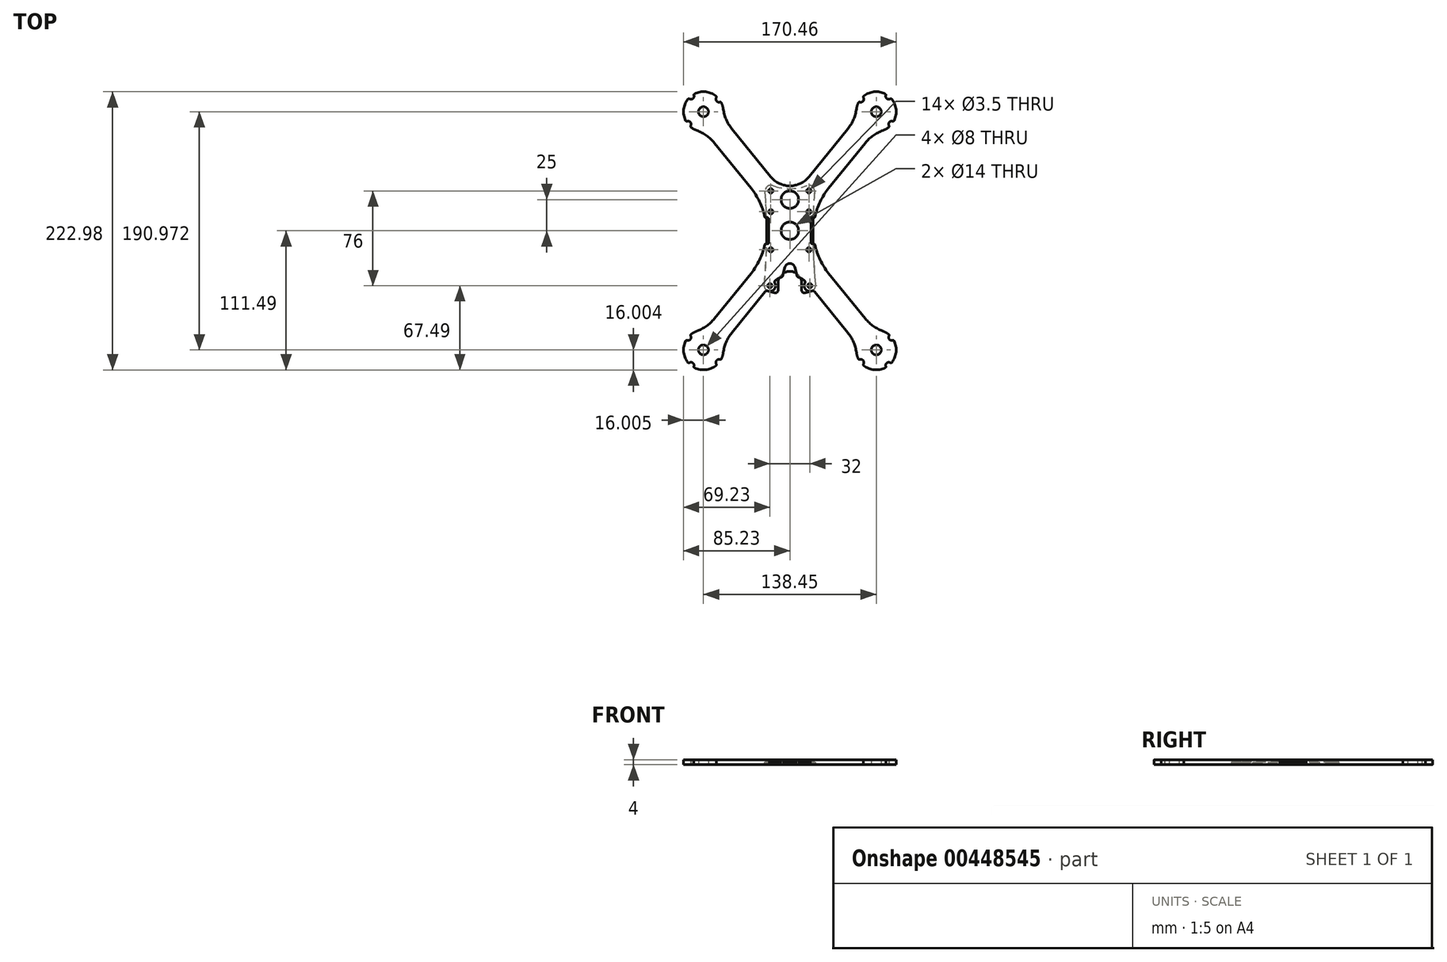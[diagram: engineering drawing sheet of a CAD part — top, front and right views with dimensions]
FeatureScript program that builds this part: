
annotation { "Feature Type Name" : "Feature", "Feature Type Description" : "" }
export const myFeature = defineFeature(function(context is Context, id is Id, definition is map)
    precondition{}
    {
        {
            var Q0;
            Q0=qCreatedBy(makeId("Top.planeOp"),FACE);
            var sketch = newSketch(context, id + "F0", { "sketchPlane" : qUnion([Q0])});
            skLineSegment(sketch, "E0", {"start": v(0, 10) * mm, "end": v(-69.23, 95.49) * mm, "construction": true});
            skCircle(sketch, "E1", {"center": v(-15.25, 32) * mm, "radius": 1.75 * mm});
            skCircle(sketch, "E2", {"center": v(-15.25, 15.25) * mm, "radius": 1.75 * mm});
            skLineSegment(sketch, "E3", {"start": v(-60.51, 70.42) * mm, "end": v(-31.06, 34.05) * mm});
            skLineSegment(sketch, "E4", {"start": v(-46.52, 81.75) * mm, "end": v(-15.44, 43.36) * mm});
            skLineSegment(sketch, "E5", {"start": v(-19.21, 10.5) * mm, "end": v(-18, 10.5) * mm});
            skArc(sketch, "E6", {"start": v(-53.37, 97.62) * mm, "mid": v(-53.93, 100.2) * mm, "end": v(-54.92, 102.64) * mm});
            skLineSegment(sketch, "E7.trimOffspring", {"start": v(-67.9, 79.54) * mm, "end": v(-67.9, 79.54) * mm});
            skCircle(sketch, "E8", {"center": v(-69.23, 95.49) * mm, "radius": 14 * mm, "construction": true});
            skCircle(sketch, "E9", {"center": v(-69.23, 95.49) * mm, "radius": 4 * mm});
            skArc(sketch, "E10", {"start": v(-20.2, 11.3) * mm, "mid": v(-24.28, 23.31) * mm, "end": v(-31.06, 34.05) * mm});
            skPoint(sketch, "E11.orphan", {"position": v(-19, 0) * mm});
            skArc(sketch, "E12", {"start": v(-15.44, 43.36) * mm, "mid": v(-8.55, 37.93) * mm, "end": v(0, 36) * mm});
            skPoint(sketch, "E13.visualSharp", {"position": v(-20.03, 10.5) * mm});
            skArc(sketch, "E13.filletArc", {"start": v(-20.2, 11.3) * mm, "mid": v(-19.84, 10.72) * mm, "end": v(-19.21, 10.5) * mm});
            skPoint(sketch, "E14.visualSharp", {"position": v(-53.9, 90.87) * mm});
            skArc(sketch, "E14.filletArc", {"start": v(-53.37, 97.62) * mm, "mid": v(-51.04, 89.22) * mm, "end": v(-46.52, 81.75) * mm});
            skPoint(sketch, "E15.visualSharp", {"position": v(-67.9, 79.54) * mm});
            skArc(sketch, "E15.filletArc", {"start": v(-60.51, 70.42) * mm, "mid": v(-66.87, 76.4) * mm, "end": v(-74.61, 80.42) * mm});
            skArc(sketch, "E16", {"start": v(-80.48, 105.72) * mm, "mid": v(-77.72, 105.98) * mm, "end": v(-76.9, 108.62) * mm});
            skArc(sketch, "E17", {"start": v(-59, 106.74) * mm, "mid": v(-58.73, 103.98) * mm, "end": v(-56.09, 103.16) * mm});
            skArc(sketch, "E18", {"start": v(-79.46, 84.23) * mm, "mid": v(-79.72, 87) * mm, "end": v(-82.36, 87.82) * mm});
            skLineSegment(sketch, "E19", {"start": v(-69.23, 95.49) * mm, "end": v(-79.3, 107.92) * mm, "construction": true});
            skLineSegment(sketch, "E20", {"start": v(-69.23, 95.49) * mm, "end": v(-56.8, 105.56) * mm, "construction": true});
            skLineSegment(sketch, "E21", {"start": v(-69.23, 95.49) * mm, "end": v(-81.66, 85.42) * mm, "construction": true});
            skArc(sketch, "E22.trimOffspring", {"start": v(-59.25, 108) * mm, "mid": v(-67.55, 111.4) * mm, "end": v(-76.38, 109.8) * mm});
            skArc(sketch, "E23.trimOffspring", {"start": v(-81.73, 105.46) * mm, "mid": v(-85.14, 97.16) * mm, "end": v(-83.54, 88.33) * mm});
            skArc(sketch, "E24.trimOffspring", {"start": v(-79.2, 82.98) * mm, "mid": v(-77.01, 81.5) * mm, "end": v(-74.61, 80.42) * mm});
            skPoint(sketch, "E25.visualSharp", {"position": v(-77.23, 109.34) * mm});
            skArc(sketch, "E25.filletArc", {"start": v(-76.38, 109.8) * mm, "mid": v(-76.85, 109.3) * mm, "end": v(-76.9, 108.62) * mm});
            skPoint(sketch, "E26.visualSharp", {"position": v(-81.1, 106.2) * mm});
            skArc(sketch, "E26.filletArc", {"start": v(-80.48, 105.72) * mm, "mid": v(-81.15, 105.82) * mm, "end": v(-81.73, 105.46) * mm});
            skPoint(sketch, "E27.visualSharp", {"position": v(-83.08, 87.48) * mm});
            skArc(sketch, "E27.filletArc", {"start": v(-83.54, 88.33) * mm, "mid": v(-83.04, 87.86) * mm, "end": v(-82.36, 87.82) * mm});
            skPoint(sketch, "E28.visualSharp", {"position": v(-79.94, 83.6) * mm});
            skArc(sketch, "E28.filletArc", {"start": v(-79.46, 84.23) * mm, "mid": v(-79.56, 83.56) * mm, "end": v(-79.2, 82.98) * mm});
            skPoint(sketch, "E29.visualSharp", {"position": v(-58.51, 107.37) * mm});
            skArc(sketch, "E29.filletArc", {"start": v(-59, 106.74) * mm, "mid": v(-58.9, 107.41) * mm, "end": v(-59.25, 108) * mm});
            skPoint(sketch, "E30.visualSharp", {"position": v(-55.37, 103.5) * mm});
            skArc(sketch, "E30.filletArc", {"start": v(-54.92, 102.64) * mm, "mid": v(-55.4, 103.11) * mm, "end": v(-56.09, 103.16) * mm});
            skLineSegment(sketch, "E31", {"start": v(-17, 9.5) * mm, "end": v(-17, 0) * mm});
            skPoint(sketch, "E32.visualSharp", {"position": v(-17, 10.5) * mm});
            skArc(sketch, "E32.filletArc", {"start": v(-17, 9.5) * mm, "mid": v(-17.3, 10.2) * mm, "end": v(-18, 10.5) * mm});
            skArc(sketch, "E33.MirrorCS", {"start": v(-83.54, -88.33) * mm, "mid": v(-83.04, -87.86) * mm, "end": v(-82.36, -87.82) * mm});
            skArc(sketch, "E34.MirrorCS", {"start": v(-59, -106.74) * mm, "mid": v(-58.9, -107.41) * mm, "end": v(-59.25, -108) * mm});
            skArc(sketch, "E35.MirrorCS", {"start": v(-80.48, -105.72) * mm, "mid": v(-81.15, -105.82) * mm, "end": v(-81.73, -105.46) * mm});
            skArc(sketch, "E36.MirrorCS", {"start": v(-79.46, -84.23) * mm, "mid": v(-79.72, -87) * mm, "end": v(-82.36, -87.82) * mm});
            skArc(sketch, "E37.MirrorCS", {"start": v(-80.48, -105.72) * mm, "mid": v(-77.72, -105.98) * mm, "end": v(-76.9, -108.62) * mm});
            skArc(sketch, "E38.MirrorCS", {"start": v(-17, -9.5) * mm, "mid": v(-17.3, -10.2) * mm, "end": v(-18, -10.5) * mm});
            skArc(sketch, "E39.MirrorCS", {"start": v(-79.46, -84.23) * mm, "mid": v(-79.56, -83.56) * mm, "end": v(-79.2, -82.98) * mm});
            skArc(sketch, "E40.MirrorCS", {"start": v(-76.38, -109.8) * mm, "mid": v(-76.85, -109.3) * mm, "end": v(-76.9, -108.62) * mm});
            skArc(sketch, "E41.MirrorCS", {"start": v(-20.2, -11.3) * mm, "mid": v(-19.84, -10.72) * mm, "end": v(-19.21, -10.5) * mm});
            skArc(sketch, "E42.MirrorCS", {"start": v(-54.92, -102.64) * mm, "mid": v(-55.4, -103.11) * mm, "end": v(-56.09, -103.16) * mm});
            skArc(sketch, "E43.MirrorCS", {"start": v(-59, -106.74) * mm, "mid": v(-58.73, -103.98) * mm, "end": v(-56.09, -103.16) * mm});
            skLineSegment(sketch, "E44.MirrorCS", {"start": v(-19.21, -10.5) * mm, "end": v(-18, -10.5) * mm});
            skArc(sketch, "E45.MirrorCS", {"start": v(-53.37, -97.62) * mm, "mid": v(-53.93, -100.2) * mm, "end": v(-54.92, -102.64) * mm});
            skArc(sketch, "E46.MirrorCS", {"start": v(-79.2, -82.98) * mm, "mid": v(-77.01, -81.5) * mm, "end": v(-74.61, -80.42) * mm});
            skCircle(sketch, "E47.MirrorC", {"center": v(-15.25, -15.25) * mm, "radius": 1.75 * mm});
            skLineSegment(sketch, "E48.MirrorCS", {"start": v(-69.23, -95.49) * mm, "end": v(-81.66, -85.42) * mm, "construction": true});
            skArc(sketch, "E49.MirrorCS", {"start": v(-53.37, -97.62) * mm, "mid": v(-51.04, -89.22) * mm, "end": v(-46.52, -81.75) * mm});
            skLineSegment(sketch, "E50.MirrorCS", {"start": v(-69.23, -95.49) * mm, "end": v(-56.8, -105.56) * mm, "construction": true});
            skLineSegment(sketch, "E51.MirrorCS", {"start": v(-17, -9.5) * mm, "end": v(-17, 0) * mm});
            skPoint(sketch, "E52.MirrorP", {"position": v(-81.1, -106.2) * mm});
            skArc(sketch, "E53.MirrorCS", {"start": v(-20.2, -11.3) * mm, "mid": v(-24.28, -23.31) * mm, "end": v(-31.06, -34.05) * mm});
            skPoint(sketch, "E54.MirrorP", {"position": v(-55.37, -103.5) * mm});
            skLineSegment(sketch, "E55.MirrorCS", {"start": v(-60.51, -70.42) * mm, "end": v(-31.06, -34.05) * mm});
            skPoint(sketch, "E56.MirrorP", {"position": v(-83.08, -87.48) * mm});
            skPoint(sketch, "E57.MirrorP", {"position": v(-53.9, -90.87) * mm});
            skPoint(sketch, "E58.MirrorP", {"position": v(-58.51, -107.37) * mm});
            skPoint(sketch, "E59.MirrorP", {"position": v(-77.23, -109.34) * mm});
            skArc(sketch, "E60.MirrorCS", {"start": v(-81.73, -105.46) * mm, "mid": v(-85.14, -97.16) * mm, "end": v(-83.54, -88.33) * mm});
            skLineSegment(sketch, "E61.MirrorCS", {"start": v(-67.9, -79.54) * mm, "end": v(-67.9, -79.54) * mm});
            skCircle(sketch, "E62.MirrorC", {"center": v(-69.23, -95.49) * mm, "radius": 14 * mm, "construction": true});
            skLineSegment(sketch, "E63.MirrorCS", {"start": v(0, -10) * mm, "end": v(-69.23, -95.49) * mm, "construction": true});
            skArc(sketch, "E64.MirrorCS", {"start": v(-60.51, -70.42) * mm, "mid": v(-66.87, -76.4) * mm, "end": v(-74.61, -80.42) * mm});
            skPoint(sketch, "E65.MirrorP", {"position": v(-67.9, -79.54) * mm});
            skPoint(sketch, "E66.MirrorP", {"position": v(-17, -10.5) * mm});
            skPoint(sketch, "E67.MirrorP", {"position": v(-79.94, -83.6) * mm});
            skArc(sketch, "E68.MirrorCS", {"start": v(-59.25, -108) * mm, "mid": v(-67.55, -111.4) * mm, "end": v(-76.38, -109.8) * mm});
            skCircle(sketch, "E69.MirrorC", {"center": v(-69.23, -95.49) * mm, "radius": 4 * mm});
            skLineSegment(sketch, "E70.MirrorCS", {"start": v(-46.52, -81.75) * mm, "end": v(-19.86, -48.82) * mm});
            skLineSegment(sketch, "E71.MirrorCS", {"start": v(-69.23, -95.49) * mm, "end": v(-79.3, -107.92) * mm, "construction": true});
            skPoint(sketch, "E72.MirrorP", {"position": v(-20.03, -10.5) * mm});
            skCircle(sketch, "E73", {"center": v(-16, -44) * mm, "radius": 1.75 * mm});
            skArc(sketch, "E74", {"start": v(-17.6, -48.2) * mm, "mid": v(-12.68, -47.04) * mm, "end": v(-11.95, -42.04) * mm});
            skLineSegment(sketch, "E75", {"start": v(0, -36) * mm, "end": v(0, 36) * mm, "construction": true});
            skArc(sketch, "E76.MirrorCS", {"start": v(-11.29, -39.52) * mm, "mid": v(-8.97, -38.14) * mm, "end": v(-6.5, -37.1) * mm});
            skPoint(sketch, "E77.orphan", {"position": v(-15.44, -43.36) * mm});
            skLineSegment(sketch, "E78", {"start": v(-5.86, -36.41) * mm, "end": v(-3.86, -29.1) * mm});
            skPoint(sketch, "E79.orphan", {"position": v(0, -36) * mm});
            skPoint(sketch, "E80.visualSharp", {"position": v(-18.8, -47.52) * mm});
            skArc(sketch, "E80.filletArc", {"start": v(-17.6, -48.2) * mm, "mid": v(-18.82, -48.15) * mm, "end": v(-19.86, -48.82) * mm});
            skPoint(sketch, "E81.visualSharp", {"position": v(-12.89, -40.75) * mm});
            skArc(sketch, "E81.filletArc", {"start": v(-11.29, -39.52) * mm, "mid": v(-12.08, -40.66) * mm, "end": v(-11.95, -42.04) * mm});
            skPoint(sketch, "E82.visualSharp", {"position": v(-6, -36.93) * mm});
            skArc(sketch, "E82.filletArc", {"start": v(-6.5, -37.1) * mm, "mid": v(-6.1, -36.83) * mm, "end": v(-5.86, -36.41) * mm});
            skArc(sketch, "E83.MirrorCS", {"start": v(17, 9.5) * mm, "mid": v(17.3, 10.2) * mm, "end": v(18, 10.5) * mm});
            skArc(sketch, "E84.MirrorCS", {"start": v(20.2, 11.3) * mm, "mid": v(19.84, 10.72) * mm, "end": v(19.21, 10.5) * mm});
            skLineSegment(sketch, "E85.MirrorCS", {"start": v(19.21, 10.5) * mm, "end": v(18, 10.5) * mm});
            skLineSegment(sketch, "E86.MirrorCS", {"start": v(19.21, -10.5) * mm, "end": v(18, -10.5) * mm});
            skArc(sketch, "E87.MirrorCS", {"start": v(59, 106.74) * mm, "mid": v(58.73, 103.98) * mm, "end": v(56.09, 103.16) * mm});
            skArc(sketch, "E88.MirrorCS", {"start": v(20.2, -11.3) * mm, "mid": v(19.84, -10.72) * mm, "end": v(19.21, -10.5) * mm});
            skArc(sketch, "E89.MirrorCS", {"start": v(83.54, 88.33) * mm, "mid": v(83.04, 87.86) * mm, "end": v(82.36, 87.82) * mm});
            skArc(sketch, "E90.MirrorCS", {"start": v(83.54, -88.33) * mm, "mid": v(83.04, -87.86) * mm, "end": v(82.36, -87.82) * mm});
            skArc(sketch, "E91.MirrorCS", {"start": v(17, -9.5) * mm, "mid": v(17.3, -10.2) * mm, "end": v(18, -10.5) * mm});
            skArc(sketch, "E92.MirrorCS", {"start": v(80.48, -105.72) * mm, "mid": v(81.15, -105.82) * mm, "end": v(81.73, -105.46) * mm});
            skArc(sketch, "E93.MirrorCS", {"start": v(17.6, -48.2) * mm, "mid": v(18.82, -48.15) * mm, "end": v(19.86, -48.82) * mm});
            skArc(sketch, "E94.MirrorCS", {"start": v(54.92, 102.64) * mm, "mid": v(55.4, 103.11) * mm, "end": v(56.09, 103.16) * mm});
            skArc(sketch, "E95.MirrorCS", {"start": v(59, 106.74) * mm, "mid": v(58.9, 107.41) * mm, "end": v(59.25, 108) * mm});
            skArc(sketch, "E96.MirrorCS", {"start": v(79.46, 84.23) * mm, "mid": v(79.72, 87) * mm, "end": v(82.36, 87.82) * mm});
            skArc(sketch, "E97.MirrorCS", {"start": v(76.38, 109.8) * mm, "mid": v(76.85, 109.3) * mm, "end": v(76.9, 108.62) * mm});
            skArc(sketch, "E98.MirrorCS", {"start": v(76.38, -109.8) * mm, "mid": v(76.85, -109.3) * mm, "end": v(76.9, -108.62) * mm});
            skArc(sketch, "E99.MirrorCS", {"start": v(54.92, -102.64) * mm, "mid": v(55.4, -103.11) * mm, "end": v(56.09, -103.16) * mm});
            skArc(sketch, "E100.MirrorCS", {"start": v(79.46, -84.23) * mm, "mid": v(79.72, -87) * mm, "end": v(82.36, -87.82) * mm});
            skArc(sketch, "E101.MirrorCS", {"start": v(6.5, -37.1) * mm, "mid": v(6.1, -36.83) * mm, "end": v(5.86, -36.41) * mm});
            skArc(sketch, "E102.MirrorCS", {"start": v(80.48, -105.72) * mm, "mid": v(77.72, -105.98) * mm, "end": v(76.9, -108.62) * mm});
            skArc(sketch, "E103.MirrorCS", {"start": v(11.29, -39.52) * mm, "mid": v(12.08, -40.66) * mm, "end": v(11.95, -42.04) * mm});
            skArc(sketch, "E104.MirrorCS", {"start": v(59, -106.74) * mm, "mid": v(58.73, -103.98) * mm, "end": v(56.09, -103.16) * mm});
            skArc(sketch, "E105.MirrorCS", {"start": v(79.46, 84.23) * mm, "mid": v(79.56, 83.56) * mm, "end": v(79.2, 82.98) * mm});
            skArc(sketch, "E106.MirrorCS", {"start": v(79.46, -84.23) * mm, "mid": v(79.56, -83.56) * mm, "end": v(79.2, -82.98) * mm});
            skArc(sketch, "E107.MirrorCS", {"start": v(80.48, 105.72) * mm, "mid": v(81.15, 105.82) * mm, "end": v(81.73, 105.46) * mm});
            skArc(sketch, "E108.MirrorCS", {"start": v(80.48, 105.72) * mm, "mid": v(77.72, 105.98) * mm, "end": v(76.9, 108.62) * mm});
            skArc(sketch, "E109.MirrorCS", {"start": v(11.29, -39.52) * mm, "mid": v(8.97, -38.14) * mm, "end": v(6.5, -37.1) * mm});
            skArc(sketch, "E110.MirrorCS", {"start": v(59, -106.74) * mm, "mid": v(58.9, -107.41) * mm, "end": v(59.25, -108) * mm});
            skCircle(sketch, "E111.MirrorC", {"center": v(16, -44) * mm, "radius": 1.75 * mm});
            skArc(sketch, "E112.MirrorCS", {"start": v(79.2, -82.98) * mm, "mid": v(77.01, -81.5) * mm, "end": v(74.61, -80.42) * mm});
            skArc(sketch, "E113.MirrorCS", {"start": v(53.37, -97.62) * mm, "mid": v(53.93, -100.2) * mm, "end": v(54.92, -102.64) * mm});
            skLineSegment(sketch, "E114.MirrorCS", {"start": v(17, -9.5) * mm, "end": v(17, 0) * mm});
            skLineSegment(sketch, "E115.MirrorCS", {"start": v(17, 9.5) * mm, "end": v(17, 0) * mm});
            skArc(sketch, "E116.MirrorCS", {"start": v(53.37, 97.62) * mm, "mid": v(53.93, 100.2) * mm, "end": v(54.92, 102.64) * mm});
            skArc(sketch, "E117.MirrorCS", {"start": v(79.2, 82.98) * mm, "mid": v(77.01, 81.5) * mm, "end": v(74.61, 80.42) * mm});
            skCircle(sketch, "E118.MirrorC", {"center": v(69.23, -95.49) * mm, "radius": 4 * mm});
            skPoint(sketch, "E119.MirrorP", {"position": v(19, 0) * mm});
            skLineSegment(sketch, "E120.MirrorCS", {"start": v(69.23, 95.49) * mm, "end": v(56.8, 105.56) * mm, "construction": true});
            skPoint(sketch, "E121.MirrorP", {"position": v(15.44, -43.36) * mm});
            skArc(sketch, "E122.MirrorCS", {"start": v(53.37, 97.62) * mm, "mid": v(51.04, 89.22) * mm, "end": v(46.52, 81.75) * mm});
            skArc(sketch, "E123.MirrorCS", {"start": v(60.51, 70.42) * mm, "mid": v(66.87, 76.4) * mm, "end": v(74.61, 80.42) * mm});
            skCircle(sketch, "E124.MirrorC", {"center": v(15.25, -15.25) * mm, "radius": 1.75 * mm});
            skArc(sketch, "E125.MirrorCS", {"start": v(60.51, -70.42) * mm, "mid": v(66.87, -76.4) * mm, "end": v(74.61, -80.42) * mm});
            skLineSegment(sketch, "E126.MirrorCS", {"start": v(69.23, 95.49) * mm, "end": v(81.66, 85.42) * mm, "construction": true});
            skCircle(sketch, "E127.MirrorC", {"center": v(15.25, 15.25) * mm, "radius": 1.75 * mm});
            skPoint(sketch, "E128.MirrorP", {"position": v(18.8, -47.52) * mm});
            skCircle(sketch, "E129.MirrorC", {"center": v(69.23, 95.49) * mm, "radius": 4 * mm});
            skArc(sketch, "E130.MirrorCS", {"start": v(17.6, -48.2) * mm, "mid": v(12.68, -47.04) * mm, "end": v(11.95, -42.04) * mm});
            skCircle(sketch, "E131.MirrorC", {"center": v(15.25, 32) * mm, "radius": 1.75 * mm});
            skArc(sketch, "E132.MirrorCS", {"start": v(53.37, -97.62) * mm, "mid": v(51.04, -89.22) * mm, "end": v(46.52, -81.75) * mm});
            skLineSegment(sketch, "E133.MirrorCS", {"start": v(69.23, -95.49) * mm, "end": v(79.3, -107.92) * mm, "construction": true});
            skLineSegment(sketch, "E134.MirrorCS", {"start": v(69.23, 95.49) * mm, "end": v(79.3, 107.92) * mm, "construction": true});
            skPoint(sketch, "E135.MirrorP", {"position": v(81.1, -106.2) * mm});
            skArc(sketch, "E136.MirrorCS", {"start": v(59.25, -108) * mm, "mid": v(67.55, -111.4) * mm, "end": v(76.38, -109.8) * mm});
            skLineSegment(sketch, "E137.MirrorCS", {"start": v(5.86, -36.41) * mm, "end": v(3.86, -29.1) * mm});
            skPoint(sketch, "E138.MirrorP", {"position": v(55.37, 103.5) * mm});
            skArc(sketch, "E139.MirrorCS", {"start": v(81.73, 105.46) * mm, "mid": v(85.14, 97.16) * mm, "end": v(83.54, 88.33) * mm});
            skPoint(sketch, "E140.MirrorP", {"position": v(20.03, 10.5) * mm});
            skLineSegment(sketch, "E141.MirrorCS", {"start": v(69.23, -95.49) * mm, "end": v(81.66, -85.42) * mm, "construction": true});
            skLineSegment(sketch, "E142.MirrorCS", {"start": v(0, -10) * mm, "end": v(69.23, -95.49) * mm, "construction": true});
            skPoint(sketch, "E143.MirrorP", {"position": v(67.9, -79.54) * mm});
            skPoint(sketch, "E144.MirrorP", {"position": v(81.1, 106.2) * mm});
            skPoint(sketch, "E145.MirrorP", {"position": v(53.9, -90.87) * mm});
            skPoint(sketch, "E146.MirrorP", {"position": v(83.08, -87.48) * mm});
            skPoint(sketch, "E147.MirrorP", {"position": v(17, -10.5) * mm});
            skPoint(sketch, "E148.MirrorP", {"position": v(6, -36.93) * mm});
            skArc(sketch, "E149.MirrorCS", {"start": v(81.73, -105.46) * mm, "mid": v(85.14, -97.16) * mm, "end": v(83.54, -88.33) * mm});
            skCircle(sketch, "E150.MirrorC", {"center": v(69.23, 95.49) * mm, "radius": 14 * mm, "construction": true});
            skLineSegment(sketch, "E151.MirrorCS", {"start": v(46.52, 81.75) * mm, "end": v(15.44, 43.36) * mm});
            skPoint(sketch, "E152.MirrorP", {"position": v(20.03, -10.5) * mm});
            skPoint(sketch, "E153.MirrorP", {"position": v(53.9, 90.87) * mm});
            skLineSegment(sketch, "E154.MirrorCS", {"start": v(67.9, -79.54) * mm, "end": v(67.9, -79.54) * mm});
            skPoint(sketch, "E155.MirrorP", {"position": v(67.9, 79.54) * mm});
            skPoint(sketch, "E156.MirrorP", {"position": v(17, 10.5) * mm});
            skPoint(sketch, "E157.MirrorP", {"position": v(77.23, -109.34) * mm});
            skPoint(sketch, "E158.MirrorP", {"position": v(77.23, 109.34) * mm});
            skLineSegment(sketch, "E159.MirrorCS", {"start": v(67.9, 79.54) * mm, "end": v(67.9, 79.54) * mm});
            skLineSegment(sketch, "E160.MirrorCS", {"start": v(46.52, -81.75) * mm, "end": v(19.86, -48.82) * mm});
            skLineSegment(sketch, "E161.MirrorCS", {"start": v(60.51, -70.42) * mm, "end": v(31.06, -34.05) * mm});
            skArc(sketch, "E162.MirrorCS", {"start": v(59.25, 108) * mm, "mid": v(67.55, 111.4) * mm, "end": v(76.38, 109.8) * mm});
            skPoint(sketch, "E163.MirrorP", {"position": v(83.08, 87.48) * mm});
            skLineSegment(sketch, "E164.MirrorCS", {"start": v(60.51, 70.42) * mm, "end": v(31.06, 34.05) * mm});
            skPoint(sketch, "E165.MirrorP", {"position": v(79.94, 83.6) * mm});
            skPoint(sketch, "E166.MirrorP", {"position": v(55.37, -103.5) * mm});
            skPoint(sketch, "E167.MirrorP", {"position": v(79.94, -83.6) * mm});
            skArc(sketch, "E168.MirrorCS", {"start": v(20.2, -11.3) * mm, "mid": v(24.28, -23.31) * mm, "end": v(31.06, -34.05) * mm});
            skArc(sketch, "E169.MirrorCS", {"start": v(20.2, 11.3) * mm, "mid": v(24.28, 23.31) * mm, "end": v(31.06, 34.05) * mm});
            skPoint(sketch, "E170.MirrorP", {"position": v(58.51, 107.37) * mm});
            skLineSegment(sketch, "E171.MirrorCS", {"start": v(69.23, -95.49) * mm, "end": v(56.8, -105.56) * mm, "construction": true});
            skPoint(sketch, "E172.MirrorP", {"position": v(58.51, -107.37) * mm});
            skCircle(sketch, "E173.MirrorC", {"center": v(69.23, -95.49) * mm, "radius": 14 * mm, "construction": true});
            skLineSegment(sketch, "E174.MirrorCS", {"start": v(0, 10) * mm, "end": v(69.23, 95.49) * mm, "construction": true});
            skPoint(sketch, "E175.MirrorP", {"position": v(12.89, -40.75) * mm});
            skArc(sketch, "E176.MirrorCS", {"start": v(15.44, 43.36) * mm, "mid": v(8.55, 37.93) * mm, "end": v(0, 36) * mm});
            skPoint(sketch, "E177.visualSharp", {"position": v(0, -15) * mm});
            skArc(sketch, "E177.filletArc", {"start": v(3.86, -29.1) * mm, "mid": v(0, -26.16) * mm, "end": v(-3.86, -29.1) * mm});
            skCircle(sketch, "E178", {"center": v(-69.23, -95.49) * mm, "radius": 64.25 * mm, "construction": true});
            skCircle(sketch, "E179.MirrorC", {"center": v(69.23, -95.49) * mm, "radius": 64.25 * mm, "construction": true});
            skCircle(sketch, "E180", {"center": v(0, 0) * mm, "radius": 7 * mm});
            skCircle(sketch, "E181", {"center": v(0, 25) * mm, "radius": 7 * mm});
            skSolve(sketch);
        }
        {
            var Q0;
            Q0=makeQuery(id+"F0.imprint","IMPRINT",FACE,{"disambiguationData":[TD([[makeQuery(id+"F0.imprint","IMPRINT",EDGE,{"derivedFrom":sQuery(id+"F0.wireOp",EDGE,"E1")}),-1.0]])]});
            extrude(context, id + "F1", {"entities" : qUnion([Q0]), "depth" : 4 * mm});
        }
        {
            var Q0;
            Q0=qCreatedBy(makeId("Top.planeOp"),FACE);
            var sketch = newSketch(context, id + "F2", { "sketchPlane" : qUnion([Q0])});
            skCircle(sketch, "E182", {"center": v(-16, -44) * mm, "radius": 1.75 * mm});
            skCircle(sketch, "E183", {"center": v(-15.25, 32) * mm, "radius": 1.75 * mm});
            skCircle(sketch, "E184", {"center": v(-15.25, -15.25) * mm, "radius": 1.75 * mm});
            skArc(sketch, "E185", {"start": v(-13.7, 36.23) * mm, "mid": v(-17.97, 35.59) * mm, "end": v(-19.74, 31.66) * mm});
            skArc(sketch, "E186", {"start": v(-20.48, -43.58) * mm, "mid": v(-19.75, -46.5) * mm, "end": v(-17.34, -48.3) * mm});
            skArc(sketch, "E187", {"start": v(-20.48, -43.58) * mm, "mid": v(-18.52, -5.97) * mm, "end": v(-19.74, 31.66) * mm});
            skLineSegment(sketch, "E188", {"start": v(-18.5, 0) * mm, "end": v(0, 0) * mm, "construction": true});
            skCircle(sketch, "E189.MirrorC", {"center": v(16, -44) * mm, "radius": 1.75 * mm});
            skArc(sketch, "E190.MirrorCS", {"start": v(20.48, -43.58) * mm, "mid": v(18.52, -5.97) * mm, "end": v(19.74, 31.66) * mm});
            skArc(sketch, "E191.MirrorC", {"start": v(20.48, -43.58) * mm, "mid": v(19.75, -46.5) * mm, "end": v(17.34, -48.3) * mm});
            skCircle(sketch, "E192.MirrorC", {"center": v(15.25, 32) * mm, "radius": 1.75 * mm});
            skArc(sketch, "E193.MirrorC", {"start": v(13.7, 36.23) * mm, "mid": v(17.97, 35.59) * mm, "end": v(19.74, 31.66) * mm});
            skCircle(sketch, "E194.MirrorC", {"center": v(15.25, -15.25) * mm, "radius": 1.75 * mm});
            skArc(sketch, "E195", {"start": v(-17.34, -48.3) * mm, "mid": v(-13.45, -49.4) * mm, "end": v(-9.5, -50.28) * mm});
            skArc(sketch, "E196.MirrorCS", {"start": v(17.34, -48.3) * mm, "mid": v(13.45, -49.4) * mm, "end": v(9.5, -50.28) * mm});
            skLineSegment(sketch, "E197", {"start": v(-9.5, -42) * mm, "end": v(-9.5, -50.28) * mm});
            skLineSegment(sketch, "E198.MirrorCS", {"start": v(9.5, -42) * mm, "end": v(9.5, -50.28) * mm});
            skArc(sketch, "E199.trimOffspring", {"start": v(9.5, -42) * mm, "mid": v(0, -32.5) * mm, "end": v(-9.5, -42) * mm});
            skArc(sketch, "E200", {"start": v(-13.7, 36.23) * mm, "mid": v(0, 33.8) * mm, "end": v(13.7, 36.23) * mm});
            skSolve(sketch);
        }
        {
            var Q0;
            Q0=makeQuery(id+"F2.imprint","IMPRINT",FACE,{"disambiguationData":[TD([[makeQuery(id+"F2.imprint","IMPRINT",EDGE,{"derivedFrom":sQuery(id+"F2.wireOp",EDGE,"E182")}),-1.0]])]});
            extrude(context, id + "F3", {"entities" : qUnion([Q0]), "depth" : 2 * mm});
        }
        {
            var Q0;
            Q0=makeQuery(id+"F3.opExtrude","SWEPT_EDGE",EDGE,{"disambiguationData":[OSD([sQuery(id+"F2.wireOp",EDGE,"E195"),sQuery(id+"F2.wireOp",EDGE,"E197")])]});
            var Q1;
            Q1=makeQuery(id+"F3.opExtrude","SWEPT_EDGE",EDGE,{"disambiguationData":[OSD([sQuery(id+"F2.wireOp",EDGE,"E196.MirrorCS"),sQuery(id+"F2.wireOp",EDGE,"E198.MirrorCS")])]});
            fillet(context, id + "F4", {"entities" : qUnion([Q0, Q1]), "radius" : 2 * mm, "tangentPropagation" : true, "allowEdgeOverflow" : false});
        }
    });
